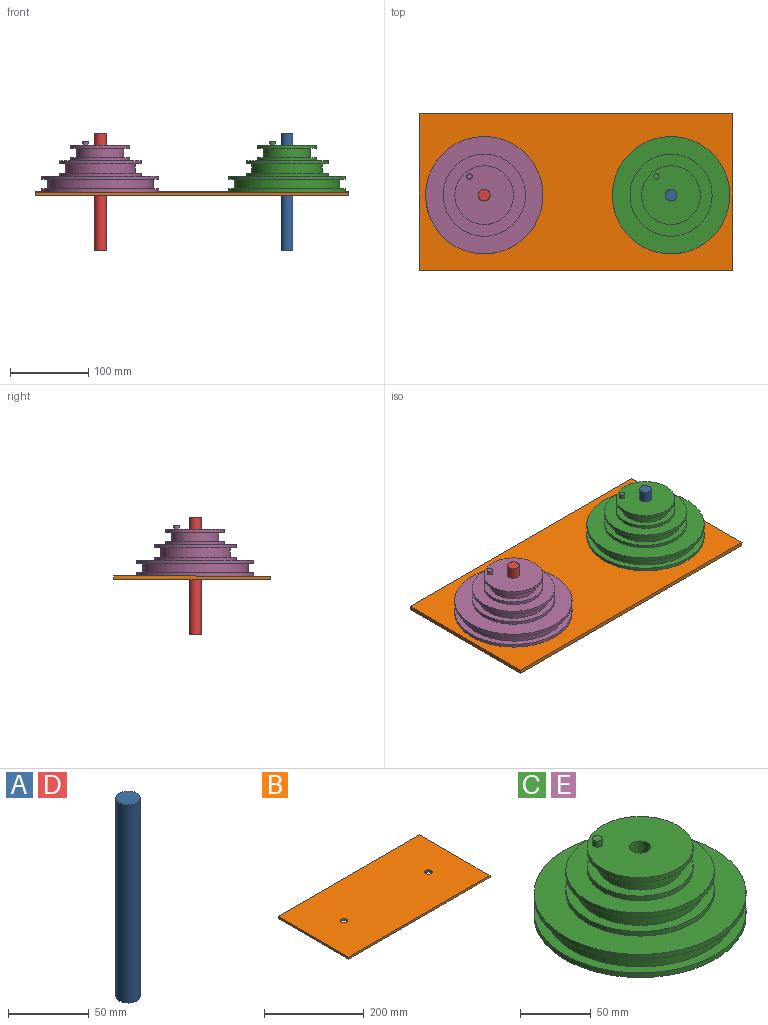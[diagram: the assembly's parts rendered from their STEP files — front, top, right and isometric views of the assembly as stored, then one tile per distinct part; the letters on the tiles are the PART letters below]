
ASSEMBLY  parts=5 mates=4
PART A: 3 faces, bbox 15x15x150 mm
  f0: cylinder r=7.5mm len=150mm, axis (0,0,-1), area 7068.6mm2, adj f1,f2
  f1: plane 15x15mm, normal (0,0,1), area 176.7mm2, adj f0
  f2: plane 15x15mm, normal (0,0,-1), area 176.7mm2, adj f0
PART B: 8 faces, bbox 400x200x5 mm
  f0: plane 200x5mm, normal (-1,0,0), area 1000mm2, adj f1,f3,f4,f5
  f1: plane 400x5mm, normal (0,-1,0), area 2000mm2, adj f0,f2,f4,f5
  f2: plane 200x5mm, normal (1,0,0), area 1000mm2, adj f1,f3,f4,f5
  f3: plane 400x5mm, normal (0,1,0), area 2000mm2, adj f0,f2,f4,f5
  f4: plane 400x200mm, normal (0,0,1), area 79646.6mm2, adj f0,f1,f2,f3,f6,f7
  f5: plane 400x200mm, normal (0,0,-1), area 79646.6mm2, adj f0,f1,f2,f3,f6,f7
  f6: cylinder r=7.5mm len=15mm, axis (0,0,-1), area 235.6mm2, adj f4,f5
  f7: cylinder r=7.5mm len=15mm, axis (0,0,-1), area 235.6mm2, adj f4,f5
PART C: 22 faces, bbox 150x150x65 mm
  f0: cylinder r=37.5mm len=75mm, axis (0,0,-1), area 942.5mm2, adj f1,f19
  f1: plane 75x75mm, normal (0,0,1), area 1590.4mm2, adj f0,f2
  f2: cylinder r=30mm len=60mm, axis (0,0,-1), area 2261.9mm2, adj f1,f5
  f3: cylinder r=37.5mm len=75mm, axis (0,0,-1), area 942.5mm2, adj f4,f5
  f4: plane 75x75mm, normal (0,0,1), area 4202mm2, adj f3,f6,f21
  f5: plane 75x75mm, normal (0,0,-1), area 1590.4mm2, adj f2,f3
  f6: cylinder r=3.53mm len=7.06mm, axis (0,0,-1), area 110.9mm2, adj f4,f7
  f7: plane 7.06x7.06mm, normal (0,0,1), area 39.1mm2, adj f6
  f8: cylinder r=75mm len=150mm, axis (0,0,-1), area 1885mm2, adj f9,f10
  f9: plane 150x150mm, normal (0,0,1), area 3357.6mm2, adj f8,f11
  f10: plane 150x150mm, normal (0,0,-1), area 17494.7mm2, adj f8,f21
  f11: cylinder r=67.5mm len=135mm, axis (0,0,-1), area 5089.4mm2, adj f9,f14
  f12: cylinder r=75mm len=150mm, axis (0,0,-1), area 1885mm2, adj f13,f14
  f13: plane 150x150mm, normal (0,0,1), area 9012.4mm2, adj f12,f15
  f14: plane 150x150mm, normal (0,0,-1), area 3357.6mm2, adj f11,f12
  f15: cylinder r=52.5mm len=105mm, axis (0,0,-1), area 1319.5mm2, adj f13,f16
  f16: plane 105x105mm, normal (0,0,1), area 2297.3mm2, adj f15,f17
  f17: cylinder r=45mm len=90mm, axis (0,0,-1), area 3392.9mm2, adj f16,f20
  f18: cylinder r=52.5mm len=105mm, axis (0,0,-1), area 1319.5mm2, adj f19,f20
  f19: plane 105x105mm, normal (0,0,1), area 4241.2mm2, adj f0,f18
  f20: plane 105x105mm, normal (0,0,-1), area 2297.3mm2, adj f17,f18
  f21: cylinder r=7.5mm len=60mm, axis (0,0,-1), area 2827.4mm2, adj f4,f10
PART D: same geometry as A
PART E: same geometry as C
PLACE A rot(axis=(-1,0,0),180deg) t=(252.09,-249.41,-104.15)mm
PLACE B t=(130.42,-249.41,-184.15)mm
PLACE C t=(252.09,-249.41,-179.15)mm
PLACE D rot(axis=(0,-1,0),180deg) t=(13.39,-249.41,-104.15)mm
PLACE E t=(13.39,-249.41,-179.15)mm
MATE fastened C.f0 <-> A.f0  axis (0,0,-1) through (252.09,-249.41,-179.15)mm
MATE fastened D.f0 <-> E.f0  axis (0,0,1) through (13.39,-249.41,-179.15)mm
MATE revolute B.f6 <-> A.f0  axis (0,0,1) through (252.09,-249.41,-179.15)mm
MATE revolute D.f0 <-> B.f7  axis (0,0,1) through (13.39,-249.41,-179.15)mm
